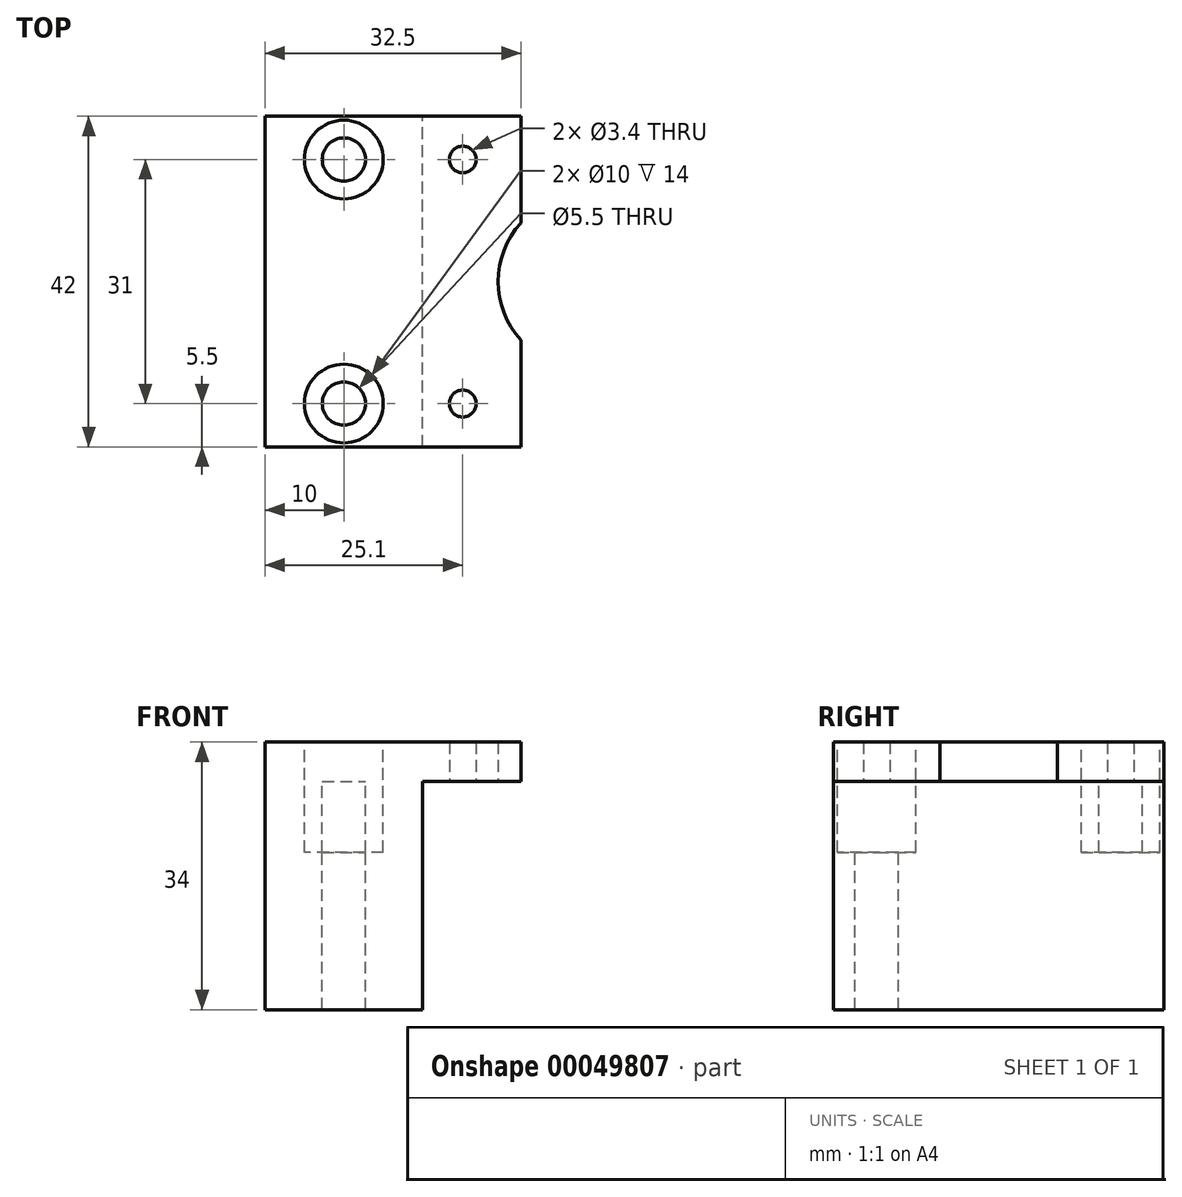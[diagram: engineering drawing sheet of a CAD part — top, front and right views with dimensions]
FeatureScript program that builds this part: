
annotation { "Feature Type Name" : "Feature", "Feature Type Description" : "" }
export const myFeature = defineFeature(function(context is Context, id is Id, definition is map)
    precondition{}
    {
        {
            var Q0;
            Q0=qCreatedBy(makeId("Front.planeOp"),FACE);
            var sketch = newSketch(context, id + "F0", { "sketchPlane" : qUnion([Q0])});
            skLineSegment(sketch, "E0", {"start": v(8.5, 5) * mm, "end": v(8.5, 5) * mm});
            skLineSegment(sketch, "E1", {"start": v(8.5, 5) * mm, "end": v(12.5, 5) * mm});
            skLineSegment(sketch, "E2", {"start": v(12.5, 5) * mm, "end": v(12.5, 0) * mm});
            skLineSegment(sketch, "E3", {"start": v(12.5, 0) * mm, "end": v(0, 0) * mm});
            skLineSegment(sketch, "E4", {"start": v(0, 0) * mm, "end": v(0, 5) * mm});
            skLineSegment(sketch, "E5", {"start": v(0, 5) * mm, "end": v(8.5, 5) * mm});
            skSolve(sketch);
        }
        {
            var Q0;
            Q0=qSketchRegion(id+"F0",true);
            extrude(context, id + "F1", {"entities" : qUnion([Q0]), "oppositeDirection" : true, "depth" : 42 * mm});
        }
        {
            var Q0;
            Q0=makeQuery(id+"F1.opExtrude","SWEPT_FACE",FACE,{"disambiguationData":[OSD([sQuery(id+"F0.wireOp",EDGE,"E3")])]});
            var sketch = newSketch(context, id + "F2", { "sketchPlane" : qUnion([Q0])});
            skCircle(sketch, "E6", {"center": v(5.1, -5.5) * mm, "radius": 1.7 * mm});
            skCircle(sketch, "E7", {"center": v(5.1, -36.5) * mm, "radius": 1.7 * mm});
            skCircle(sketch, "E8", {"center": v(20.6, -21) * mm, "radius": 11 * mm});
            skLineSegment(sketch, "E9", {"start": v(0, -21) * mm, "end": v(12.5, -21) * mm, "construction": true});
            skSolve(sketch);
        }
        {
            var Q0;
            Q0=qSketchRegion(id+"F2",true);
            extrude(context, id + "F3", {"entities" : qUnion([Q0]), "operationType" : NewBodyOperationType.REMOVE, "endBound" : BoundingType.THROUGH_ALL, "oppositeDirection" : true, "depth" : 25 * mm});
        }
        {
            var Q0;
            Q0=makeQuery(id+"F1.opExtrude","SWEPT_FACE",FACE,{"disambiguationData":[OSD([sQuery(id+"F0.wireOp",EDGE,"E4")])]});
            var sketch = newSketch(context, id + "F4", { "sketchPlane" : qUnion([Q0])});
            skLineSegment(sketch, "E10.bottom", {"start": v(-42, 5) * mm, "end": v(0, 5) * mm});
            skLineSegment(sketch, "E10.top", {"start": v(-42, 0) * mm, "end": v(0, 0) * mm});
            skLineSegment(sketch, "E10.left", {"start": v(-42, 5) * mm, "end": v(-42, 0) * mm});
            skLineSegment(sketch, "E10.right", {"start": v(0, 5) * mm, "end": v(0, 0) * mm});
            skSolve(sketch);
        }
        {
            var Q0;
            Q0=qSketchRegion(id+"F4",true);
            extrude(context, id + "F5", {"entities" : qUnion([Q0]), "operationType" : NewBodyOperationType.ADD, "depth" : 20 * mm});
        }
        {
            var Q0;
            Q0=makeQuery(id+"F5.boolean.opBoolean","MERGE",FACE,{"derivedFrom":[makeQuery(id+"F1.opExtrude","SWEPT_FACE",FACE,{"disambiguationData":[OSD([sQuery(id+"F0.wireOp",EDGE,"E5")])]}),makeQuery(id+"F5.opExtrude","SWEPT_FACE",FACE,{"disambiguationData":[OSD([sQuery(id+"F4.wireOp",EDGE,"E10.bottom")])]})]});
            var sketch = newSketch(context, id + "F6", { "sketchPlane" : qUnion([Q0])});
            skCircle(sketch, "E11", {"center": v(-10, 36.5) * mm, "radius": 2.75 * mm});
            skCircle(sketch, "E12", {"center": v(-10, 5.5) * mm, "radius": 2.75 * mm});
            skPoint(sketch, "E13", {"position": v(5.1, 36.5) * mm});
            skPoint(sketch, "E14", {"position": v(5.1, 5.5) * mm});
            skCircle(sketch, "E15", {"center": v(-10, 36.5) * mm, "radius": 5 * mm});
            skCircle(sketch, "E16", {"center": v(-10, 5.5) * mm, "radius": 5 * mm});
            skSolve(sketch);
        }
        {
            var Q0;
            Q0=qSketchRegion(id+"F6",true);
            var Q1;
            Q1=makeQuery(id+"F6.imprint","IMPRINT",FACE,{"disambiguationData":[TD([[makeQuery(id+"F6.imprint","IMPRINT",EDGE,{"derivedFrom":sQuery(id+"F6.wireOp",EDGE,"E12")}),1.0]])]});
            var Q2;
            Q2=makeQuery(id+"F6.imprint","IMPRINT",FACE,{"disambiguationData":[TD([[makeQuery(id+"F6.imprint","IMPRINT",EDGE,{"derivedFrom":sQuery(id+"F6.wireOp",EDGE,"E11")}),1.0]])]});
            extrude(context, id + "F7", {"entities" : qUnion([Q0, Q1, Q2]), "operationType" : NewBodyOperationType.REMOVE, "oppositeDirection" : true, "depth" : 19 * mm});
        }
        {
            var Q0;
            Q0=makeQuery(id+"F5.boolean.opBoolean","MERGE",FACE,{"derivedFrom":[makeQuery(id+"F1.opExtrude","SWEPT_FACE",FACE,{"disambiguationData":[OSD([sQuery(id+"F0.wireOp",EDGE,"E3")])]}),makeQuery(id+"F5.opExtrude","SWEPT_FACE",FACE,{"disambiguationData":[OSD([sQuery(id+"F4.wireOp",EDGE,"E10.top")])]})]});
            var sketch = newSketch(context, id + "F8", { "sketchPlane" : qUnion([Q0])});
            skLineSegment(sketch, "E17.bottom", {"start": v(-20, 0) * mm, "end": v(0, 0) * mm});
            skLineSegment(sketch, "E17.top", {"start": v(-20, -42) * mm, "end": v(0, -42) * mm});
            skLineSegment(sketch, "E17.left", {"start": v(-20, 0) * mm, "end": v(-20, -42) * mm});
            skLineSegment(sketch, "E17.right", {"start": v(0, 0) * mm, "end": v(0, -42) * mm});
            skCircle(sketch, "E18", {"center": v(-10, -36.5) * mm, "radius": 2.75 * mm});
            skCircle(sketch, "E19", {"center": v(-10, -36.5) * mm, "radius": 5 * mm});
            skCircle(sketch, "E20", {"center": v(-10, -5.5) * mm, "radius": 2.75 * mm});
            skSolve(sketch);
        }
        {
            var Q0;
            Q0 = qSketchRegion(id + "F8", true);
            var Q1;
            Q1=makeQuery(id+"F8.imprint","IMPRINT",FACE,{"disambiguationData":[TD([[makeQuery(id+"F8.imprint","IMPRINT",EDGE,{"derivedFrom":sQuery(id+"F8.wireOp",EDGE,"E18")}),1.0]])]});
            var Q2;
            Q2=makeQuery(id+"F8.imprint","IMPRINT",FACE,{"disambiguationData":[TD([[makeQuery(id+"F8.imprint","IMPRINT",EDGE,{"derivedFrom":sQuery(id+"F8.wireOp",EDGE,"E18")}),-1.0]])]});
            extrude(context, id + "F9", {"entities" : qUnion([Q0, Q1, Q2]), "operationType" : NewBodyOperationType.ADD, "depth" : 29 * mm});
        }
        {
            var Q0;
            Q0=makeQuery(id+"F8.imprint","IMPRINT",FACE,{"disambiguationData":[TD([[makeQuery(id+"F8.imprint","IMPRINT",EDGE,{"derivedFrom":sQuery(id+"F8.wireOp",EDGE,"E18")}),-1.0]])]});
            var Q1;
            Q1=makeQuery(id+"F8.imprint","IMPRINT",FACE,{"disambiguationData":[TD([[makeQuery(id+"F8.imprint","IMPRINT",EDGE,{"derivedFrom":sQuery(id+"F8.wireOp",EDGE,"E20")}),-1.0]])]});
            extrude(context, id + "F10", {"entities" : qUnion([Q0, Q1]), "operationType" : NewBodyOperationType.REMOVE, "depth" : 9 * mm});
        }
    });
